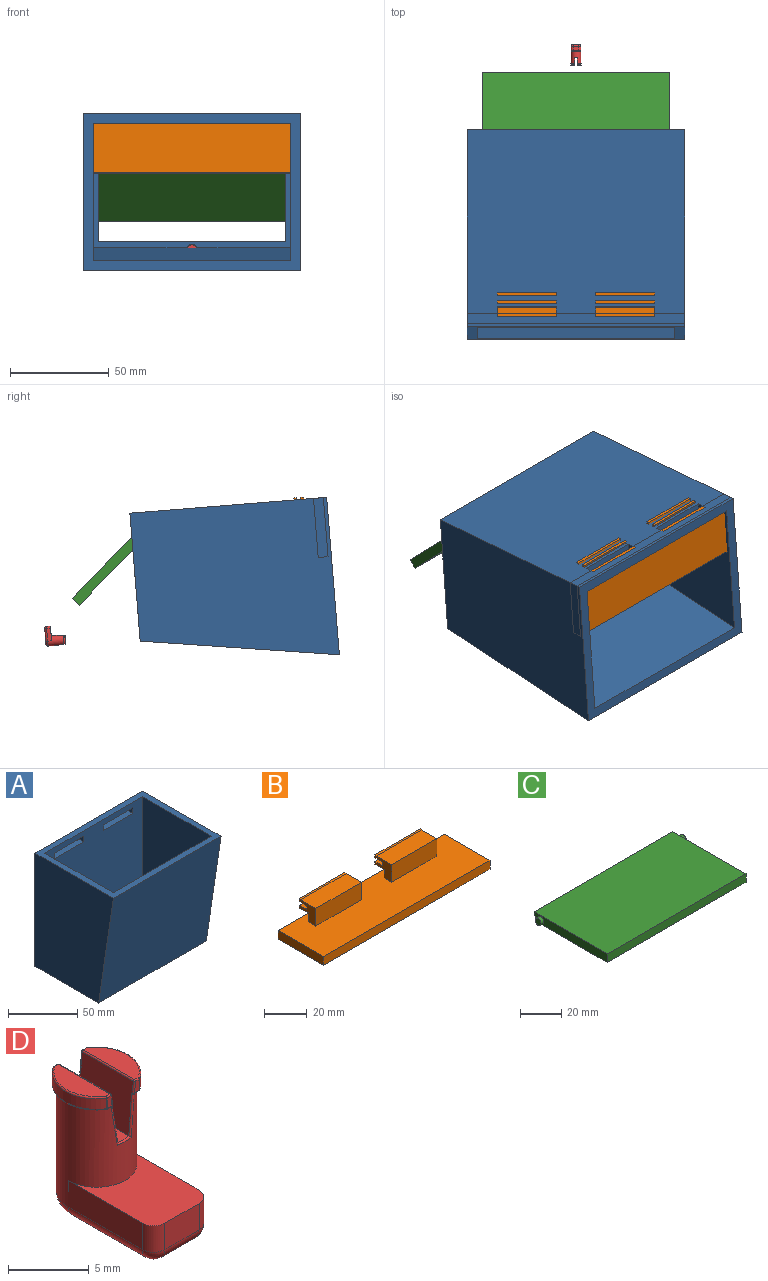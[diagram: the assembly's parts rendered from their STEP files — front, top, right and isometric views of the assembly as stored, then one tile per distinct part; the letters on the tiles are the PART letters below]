
ASSEMBLY  parts=4 mates=3
PART A: 35 faces, bbox 110x80x100 mm
  f0: plane 100x55.69mm, normal (0,0,1), area 796.4mm2, adj f3,f8,f9,f10,f19,f20,f21,f22
  f1: plane 110x65mm, normal (0,0,-1), area 2380.4mm2, adj f2,f5,f6,f7,f19,f20,f21,f22
  f2: plane 110x100mm, normal (0,1,0), area 10700mm2, adj f1,f4,f5,f6,f11,f12,f13,f14
  f3: plane 100x95mm, normal (0,-1,0), area 9200mm2, adj f0,f4,f8,f9,f11,f12,f13,f14
  f4: plane 110x80mm, normal (0,0,1), area 1805.6mm2, adj f2,f3,f5,f6,f7,f8,f9,f10
  f5: plane 100x80mm, normal (1,0,0), area 7250mm2, adj f1,f2,f4,f7
  f6: plane 100x80mm, normal (-1,0,0), area 7250mm2, adj f1,f2,f4,f7
  f7: plane 110x100mm, normal (0,-0.99,-0.15), area 11123.1mm2, adj f1,f4,f5,f6
  f8: plane 95x69.94mm, normal (-1,0,0), area 5967.8mm2, adj f0,f3,f4,f10
  f9: plane 95x69.94mm, normal (1,0,0), area 5967.8mm2, adj f0,f3,f4,f10
  f10: plane 100x95mm, normal (0,0.99,0.15), area 9595.3mm2, adj f0,f4,f8,f9,f31,f32,f33,f34
  f11: plane 30x5mm, normal (0,0,1), area 150mm2, adj f2,f3,f12,f14
  f12: plane 5x5mm, normal (1,0,0), area 25mm2, adj f2,f3,f11,f13
  f13: plane 30x5mm, normal (0,0,-1), area 150mm2, adj f2,f3,f12,f14
  f14: plane 5x5mm, normal (-1,0,0), area 25mm2, adj f2,f3,f11,f13
  f15: plane 30x5mm, normal (0,0,1), area 150mm2, adj f2,f3,f16,f18
  f16: plane 5x5mm, normal (1,0,0), area 25mm2, adj f2,f3,f15,f17
  f17: plane 30x5mm, normal (0,0,-1), area 150mm2, adj f2,f3,f16,f18
  f18: plane 5x5mm, normal (-1,0,0), area 25mm2, adj f2,f3,f15,f17
  f19: plane 95x5mm, normal (0,-1,0), area 475mm2, adj f0,f1,f20,f22
  f20: plane 50x5mm, normal (-1,0,0), area 233.7mm2, adj f0,f1,f19,f21,f23,f24,f25
  f21: plane 95x5mm, normal (0,1,0), area 475mm2, adj f0,f1,f20,f22
  f22: plane 50x5mm, normal (1,0,0), area 233.7mm2, adj f0,f1,f19,f21,f27,f28,f29
  f23: plane 2.69x2mm, normal (0,-1,0), area 5.4mm2, adj f0,f20,f24,f26
  f24: cylinder r=2mm len=3.99mm, axis (-1,0,0), area 12.2mm2, adj f20,f23,f25,f26
  f25: plane 2.47x2mm, normal (0,1,0), area 4.9mm2, adj f0,f20,f24,f26
  f26: plane 4.5x3.99mm, normal (-1,0,0), area 16.3mm2, adj f0,f23,f24,f25
  f27: cylinder r=2mm len=4mm, axis (1,0,0), area 12.6mm2, adj f22,f28,f29,f30
  f28: plane 2.5x2mm, normal (0,-1,0), area 5mm2, adj f0,f22,f27,f30
  f29: plane 2.5x2mm, normal (0,1,0), area 5mm2, adj f0,f22,f27,f30
  f30: plane 4.5x4mm, normal (1,0,0), area 16.3mm2, adj f0,f27,f28,f29
  f31: cylinder r=2.5mm len=6mm, axis (0,0,-1), area 87.4mm2, adj f0,f1,f10,f32
  f32: plane 6x3.42mm, normal (0,0,1), area 4.7mm2, adj f10,f31,f33
  f33: cylinder r=3mm len=6mm, axis (0,0,-1), area 10.1mm2, adj f10,f32,f34
  f34: plane 6x3.27mm, normal (0,0,-1), area 15.8mm2, adj f10,f33
PART B: 32 faces, bbox 110x31x15.2 mm
  f0: plane 30x1.5mm, normal (0,1,0), area 45mm2, adj f1,f17,f27,f31
  f1: plane 11x10.2mm, normal (1,0,0), area 69.5mm2, adj f0,f2,f6,f15,f16,f18,f21,f27
  f2: plane 30x5mm, normal (0,0,-1), area 150mm2, adj f1,f16,f17,f28
  f3: plane 30x1.5mm, normal (0,1,0), area 45mm2, adj f4,f14,f22,f26
  f4: plane 11x10.2mm, normal (1,0,0), area 69.5mm2, adj f3,f5,f6,f12,f13,f19,f20,f22
  f5: plane 30x10mm, normal (0,0,1), area 300mm2, adj f4,f12,f14,f23
  f6: plane 110x30mm, normal (0,0,1), area 3000mm2, adj f1,f4,f7,f8,f9,f10,f12,f13
  f7: plane 110x5mm, normal (0,-1,0), area 550mm2, adj f6,f8,f10,f11
  f8: plane 30x5mm, normal (1,0,0), area 150mm2, adj f6,f7,f9,f11
  f9: plane 110x5mm, normal (0,1,0), area 550mm2, adj f6,f8,f10,f11
  f10: plane 30x5mm, normal (-1,0,0), area 150mm2, adj f6,f7,f9,f11
  f11: plane 110x30mm, normal (0,0,-1), area 3300mm2, adj f7,f8,f9,f10
  f12: plane 30x10mm, normal (0,-1,0), area 300mm2, adj f4,f5,f6,f14
  f13: plane 30x5mm, normal (0,1,0), area 150mm2, adj f4,f6,f14,f19
  f14: plane 11x10.2mm, normal (-1,0,0), area 69.5mm2, adj f3,f5,f6,f12,f13,f19,f20,f22
  f15: plane 30x10mm, normal (0,-1,0), area 300mm2, adj f1,f6,f17,f18
  f16: plane 30x5mm, normal (0,1,0), area 150mm2, adj f1,f2,f6,f17
  f17: plane 11x10.2mm, normal (-1,0,0), area 69.5mm2, adj f0,f2,f6,f15,f16,f18,f21,f27
  f18: plane 30x10mm, normal (0,0,1), area 300mm2, adj f1,f15,f17,f27
  f19: plane 30x5mm, normal (0,0,-1), area 150mm2, adj f4,f13,f14,f22
  f20: plane 30x1.5mm, normal (0,1,0), area 45mm2, adj f4,f14,f23,f25
  f21: plane 30x1.5mm, normal (0,1,0), area 45mm2, adj f1,f17,f28,f30
  f22: plane 30x1mm, normal (0,-0.2,-0.98), area 30.6mm2, adj f3,f4,f14,f19
  f23: plane 30x1mm, normal (0,-0.2,0.98), area 30.6mm2, adj f4,f5,f14,f20
  f24: plane 30x2mm, normal (0,1,0), area 60mm2, adj f4,f14,f25,f26
  f25: plane 30x4.86mm, normal (0,0.04,-1), area 145.8mm2, adj f4,f14,f20,f24
  f26: plane 30x4.86mm, normal (0,0.04,1), area 145.8mm2, adj f3,f4,f14,f24
  f27: plane 30x1mm, normal (0,-0.2,0.98), area 30.6mm2, adj f0,f1,f17,f18
  f28: plane 30x1mm, normal (0,-0.2,-0.98), area 30.6mm2, adj f1,f2,f17,f21
  f29: plane 30x2mm, normal (0,1,0), area 60mm2, adj f1,f17,f30,f31
  f30: plane 30x4.87mm, normal (0,0.04,1), area 146.3mm2, adj f1,f17,f21,f29
  f31: plane 30x4.87mm, normal (0,0.04,-1), area 146.3mm2, adj f0,f1,f17,f29
PART C: 11 faces, bbox 99.1x50x5 mm
  f0: plane 95x5mm, normal (0,-1,0), area 475mm2, adj f1,f3,f4,f5
  f1: plane 50x5mm, normal (1,0,0), area 231.3mm2, adj f0,f2,f4,f5,f6,f10
  f2: plane 95x1.5mm, normal (0,1,0), area 142.5mm2, adj f1,f3,f4,f10
  f3: plane 50x5mm, normal (-1,0,0), area 231.3mm2, adj f0,f2,f4,f5,f8,f10
  f4: plane 95x50mm, normal (0,0,1), area 4750mm2, adj f0,f1,f2,f3
  f5: plane 95x46.5mm, normal (0,0,-1), area 4417.5mm2, adj f0,f1,f3,f10
  f6: cylinder r=2mm len=4mm, axis (-1,0,0), area 26.4mm2, adj f1,f7
  f7: plane 4x4mm, normal (1,0,0), area 12.6mm2, adj f6
  f8: cylinder r=2mm len=4mm, axis (1,0,0), area 25.1mm2, adj f3,f9
  f9: plane 4x4mm, normal (-1,0,0), area 12.6mm2, adj f8
  f10: plane 95x3.5mm, normal (0,0.71,-0.71), area 470.2mm2, adj f1,f2,f3,f5
PART D: 71 faces, bbox 6x10.2x11.6 mm
  f0: plane 4.49x1.55mm, normal (0,0,-1), area 0.8mm2, adj f17,f18,f54,f64
  f1: plane 0.05x0.02mm, normal (0,0,-1), area 0mm2, adj f10,f33,f64
  f2: plane 0.05x0.01mm, normal (0,0,-1), area 0mm2, adj f11,f37,f48
  f3: plane 4.49x1.55mm, normal (0,0,-1), area 0.8mm2, adj f12,f18,f48,f62
  f4: cylinder r=2.75mm len=4.66mm, axis (0,0,-1), area 4.4mm2, adj f15,f17,f50,f68
  f5: cylinder r=2.75mm len=4.66mm, axis (0,0,-1), area 4.4mm2, adj f12,f14,f44,f58
  f6: plane 4.49x1.56mm, normal (0,0,1), area 5.4mm2, adj f15,f16,f53,f69
  f7: plane 4.49x1.56mm, normal (0,0,1), area 5.4mm2, adj f13,f14,f45,f59
  f8: plane 0.05x0.01mm, normal (0,0,-1), area 0mm2, adj f10,f36,f54
  f9: plane 0.05x0.02mm, normal (0,0,-1), area 0mm2, adj f11,f34,f62
  f10: plane 4.65x3.86mm, normal (0.99,0,0.12), area 17.6mm2, adj f1,f8,f16,f19,f33,f36,f56,f65
  f11: plane 4.65x3.86mm, normal (-0.99,0,0.12), area 17.6mm2, adj f2,f9,f13,f19,f34,f37,f49,f63
  f12: torus R=2.65mm, axis (0,0,1), area 0.9mm2, adj f3,f5,f46,f60
  f13: cylinder r=0.1mm len=4.49mm, axis (0,-1,0), area 0.6mm2, adj f7,f11,f47,f61
  f14: torus R=2.65mm, axis (0,0,1), area 0.9mm2, adj f5,f7,f43,f57
  f15: torus R=2.65mm, axis (0,0,1), area 0.9mm2, adj f4,f6,f51,f70
  f16: cylinder r=0.1mm len=4.49mm, axis (0,1,0), area 0.6mm2, adj f6,f10,f55,f67
  f17: torus R=2.65mm, axis (0,0,1), area 0.9mm2, adj f0,f4,f52,f66
  f18: cylinder r=2.5mm len=8.01mm, axis (0,0,-1), area 99.8mm2, adj f0,f3,f20,f22,f24,f30,f33,f34
  f19: plane 4.8x1.01mm, normal (0,0,1), area 4.8mm2, adj f10,f11,f33,f34,f35,f36,f37,f38
  f20: plane 6.5x2mm, normal (1,0,0), area 13mm2, adj f18,f24,f29,f32
  f21: plane 3x2mm, normal (0,-1,0), area 6mm2, adj f24,f25,f28,f29
  f22: plane 6.5x2mm, normal (-1,0,0), area 13mm2, adj f18,f24,f25,f27
  f23: plane 8x3mm, normal (0,0,-1), area 23mm2, adj f27,f28,f30,f32
  f24: plane 7.5x5mm, normal (0,0,1), area 27.3mm2, adj f18,f20,f21,f22,f25,f29
  f25: cylinder r=1mm len=2mm, axis (0,0,1), area 3.1mm2, adj f21,f22,f24,f26
  f26: sphere r=1mm, area 1.6mm2, adj f25,f27,f28
  f27: cylinder r=1mm len=6.5mm, axis (0,-1,0), area 10.2mm2, adj f22,f23,f26,f30
  f28: cylinder r=1mm len=3mm, axis (1,0,0), area 4.7mm2, adj f21,f23,f26,f31
  f29: cylinder r=1mm len=2mm, axis (0,0,-1), area 3.1mm2, adj f20,f21,f24,f31
  f30: torus R=1.5mm, axis (0,0,-1), area 10.5mm2, adj f18,f23,f27,f32
  f31: sphere r=1mm, area 1.6mm2, adj f28,f29,f32
  f32: cylinder r=1mm len=6.5mm, axis (0,1,0), area 10.2mm2, adj f20,f23,f30,f31
  f33: bspline ~8.61x1.24mm, area 0.6mm2, adj f1,f10,f18,f19,f35,f64
  f34: bspline ~8.61x1.24mm, area 0.6mm2, adj f9,f11,f18,f19,f35,f62
  f35: torus R=2.4mm, axis (0,0,-1), area 0.2mm2, adj f18,f19,f33,f34
  f36: bspline ~8.61x1.24mm, area 0.6mm2, adj f8,f10,f18,f19,f38,f54
  f37: bspline ~8.61x1.24mm, area 0.6mm2, adj f2,f11,f18,f19,f38,f48
  f38: torus R=2.4mm, axis (0,0,-1), area 0.2mm2, adj f18,f19,f36,f37
  f39: plane 0.8x0.42mm, normal (0,-1,0), area 0.3mm2, adj f64,f65,f68,f69
  f40: plane 0.8x0.43mm, normal (0,1,0), area 0.3mm2, adj f50,f53,f54,f56
  f41: plane 0.8x0.42mm, normal (0,-1,0), area 0.3mm2, adj f58,f59,f62,f63
  f42: plane 0.8x0.43mm, normal (0,1,0), area 0.3mm2, adj f44,f45,f48,f49
  f43: sphere r=0.1mm, area 0mm2, adj f14,f44,f45
  f44: cylinder r=0.1mm len=0.8mm, axis (0,0,-1), area 0mm2, adj f5,f42,f43,f46
  f45: cylinder r=0.1mm len=0.33mm, axis (-1,0,0), area 0.1mm2, adj f7,f42,f43,f47
  f46: sphere r=0.1mm, area 0mm2, adj f12,f44,f48
  f47: sphere r=0.1mm, area 0mm2, adj f13,f45,f49
  f48: cylinder r=0.1mm len=0.54mm, axis (1,0,0), area 0.1mm2, adj f2,f3,f18,f37,f42,f46,f49
  f49: cylinder r=0.1mm len=0.93mm, axis (-0.12,0,-0.99), area 0.1mm2, adj f11,f42,f47,f48
  f50: cylinder r=0.1mm len=0.8mm, axis (0,0,-1), area 0mm2, adj f4,f40,f51,f52
  f51: sphere r=0.1mm, area 0mm2, adj f15,f50,f53
  f52: sphere r=0.1mm, area 0mm2, adj f17,f50,f54
  f53: cylinder r=0.1mm len=0.33mm, axis (-1,0,0), area 0.1mm2, adj f6,f40,f51,f55
  f54: cylinder r=0.1mm len=0.54mm, axis (1,0,0), area 0.1mm2, adj f0,f8,f18,f36,f40,f52,f56
  f55: sphere r=0.1mm, area 0mm2, adj f16,f53,f56
  f56: cylinder r=0.1mm len=0.93mm, axis (-0.12,0,0.99), area 0.1mm2, adj f10,f40,f54,f55
  f57: sphere r=0.1mm, area 0mm2, adj f14,f58,f59
  f58: cylinder r=0.1mm len=0.8mm, axis (0,0,-1), area 0mm2, adj f5,f41,f57,f60
  f59: cylinder r=0.1mm len=0.32mm, axis (1,0,0), area 0.1mm2, adj f7,f41,f57,f61
  f60: sphere r=0.1mm, area 0mm2, adj f12,f58,f62
  f61: sphere r=0.1mm, area 0mm2, adj f13,f59,f63
  f62: cylinder r=0.1mm len=0.53mm, axis (-1,0,0), area 0.1mm2, adj f3,f9,f18,f34,f41,f60,f63
  f63: cylinder r=0.1mm len=0.93mm, axis (0.12,0,0.99), area 0.1mm2, adj f11,f41,f61,f62
  f64: cylinder r=0.1mm len=0.53mm, axis (-1,0,0), area 0.1mm2, adj f0,f1,f18,f33,f39,f65,f66
  f65: cylinder r=0.1mm len=0.93mm, axis (0.12,0,-0.99), area 0.1mm2, adj f10,f39,f64,f67
  f66: sphere r=0.1mm, area 0mm2, adj f17,f64,f68
  f67: sphere r=0.1mm, area 0mm2, adj f16,f65,f69
  f68: cylinder r=0.1mm len=0.8mm, axis (0,0,-1), area 0mm2, adj f4,f39,f66,f70
  f69: cylinder r=0.1mm len=0.32mm, axis (1,0,0), area 0.1mm2, adj f6,f39,f67,f70
  f70: sphere r=0.1mm, area 0mm2, adj f15,f68,f69
PLACE A rot(axis=(1,0,0),85.4deg) t=(39.54,30.21,99.44)mm
PLACE B rot(axis=(0,-0.73,-0.68),180deg) t=(39.54,-65.77,132.25)mm
PLACE C rot(axis=(1,0,0),134deg) t=(39.54,45.3,114.17)mm
PLACE D rot(axis=(0,0.68,-0.73),180deg) t=(39.54,70.09,74.9)mm
MATE slider A.f4 <-> B.f6  axis (0,-1,0.08) through (39.54,-66.26,147.34)mm
MATE revolute C.f8 <-> A.f30  axis (-1,0,0) through (-9.96,29.47,126.95)mm
MATE slider D.f35 <-> A.f31  axis (0,-1,0.08) through (39.54,70.04,74.9)mm
